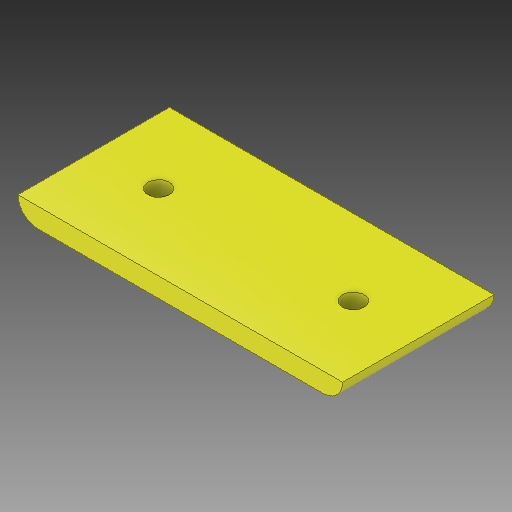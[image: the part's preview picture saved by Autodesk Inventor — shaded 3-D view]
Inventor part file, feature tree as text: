
AUTODESK INVENTOR PART (.ipt)
format: ipt  version: 2018 (Build 220112000, 112)  size: 109,056 bytes
history: native  units: mm
features: sketch x2, extrude x1, hole x1
ambient origin geometry x8: Origin, YZ Plane, XZ Plane, XY Plane, X Axis, Y Axis, Z Axis, Center Point
bodies: Solido1 (feature_tree)
feature tree (4):
  extrude  "Estrusione1"  Depth=150.0mm
  hole  "Foro1"  [1 undecoded]
  sketch  "Schizzo1"
  sketch  "Schizzo2"
note: 1 required parameter value undecoded (feature->parameter linkage not recoverable at this tier; creation-order binding heuristic only, values carry confidence <= 0.55)
